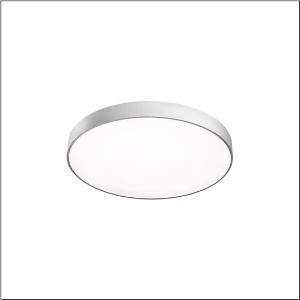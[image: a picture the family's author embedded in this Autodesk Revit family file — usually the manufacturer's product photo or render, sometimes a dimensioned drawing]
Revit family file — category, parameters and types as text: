
# Revit family: round_21_m_51mr36gm8321s
name_source: partatom
category: Lighting Fixtures
units: mm (PartAtom-declared; Revit-internal decimal feet)

## family parameters
Cut with Voids When Loaded = No
Host = Face
Light Source = No
Part Type = Normal
Room Calculation Point = No
Round Connector Dimension = Use Diameter
Shared = No

## types (1)
- --- (1 x LED, 7820 lm, 60.8 W, 3000K)
    Apparent Load = 61 VA
    CIE Flux Codes = 49 80 96 85 100
    Color Rendering = 80
    Color Temperature = 3000K
    Default Elevation = 1800 mm
    Description = Round 21 M, wall and ceiling luminaire, primary optical cover: cover, of PMMA, opal, light emission: direct/indirect distribution, primary light characteristic: symmetric, installation type: suspended mounting, surface-mounted, LED, rated luminous flux: 7.820lm, luminous efficacy: 129lm/W, light colour: 830, colour temperature: 3000K, with terminal, 3-pole, mains connection: 230V, AC, 50/60Hz, rated input power: 61W, housing, of aluminium, coated, silver, diameter: 600mm, height: 62mm, protection rating (complete): IP40, insulation class (complete): insulation class I (protective earthing), certification: CE, impact resistance: IK04, permissible operating ambient temperature: -10..+35°C, packaging unit: 1 piece
    Height = 87 mm
    Lamp = 1 x LED
    Lamp Light Flux = 7820 lm
    Lamp Power = 60.8 W
    Lamp count = 1
    Length = 600 mm
    Luminous efficacy = 129 lm/W
    Manufacturer = Siteco
    ModVariant = No
    Model = 51MR36GM8321S
    Mounting Place = Ceiling
    Mounting Type = Surface mounted
    Number of Poles = 1
    OnlyDefault = Yes
    Power Factor = 1
    Product Name = Round 21 M
    Product group = wall and ceiling luminaire
    ProductGroupID = 301
    Protection Class = Protection class I
    Protection Degree = IP 40
    RLX_Detail_Level = 1
    RLX_Emergency_Light_Flux = 0 lm
    RLX_Emergency_Type = 0
    RLX_Emergency_Type_DB = No
    RlxData = <blob elided: 17849 chars, md5=cab1c377>
    Socket = socket
    Standby Power = 0 W
    System Light Flux = 7820 lm
    System Power = 61 W
    Type Comments = factory setting: luminous flux: 100 % | (ON | ON | ON | ON) | 700 mA
    Type Image = l_1258303.jpg
    URL = http://relux.com
    VarID = @adj_013145
    Voltage = 0 V
    Weight = 0.00 kg
    Width = 0 mm  [stored 0 ft]

note: [stored X ft] marks values corroborated as IEEE doubles in the binary element streams (Revit-internal decimal feet)

## geometry (parser evidence)
native form markers: Blend x4, Sweep x12
no freeform markers — native parametric forms only
